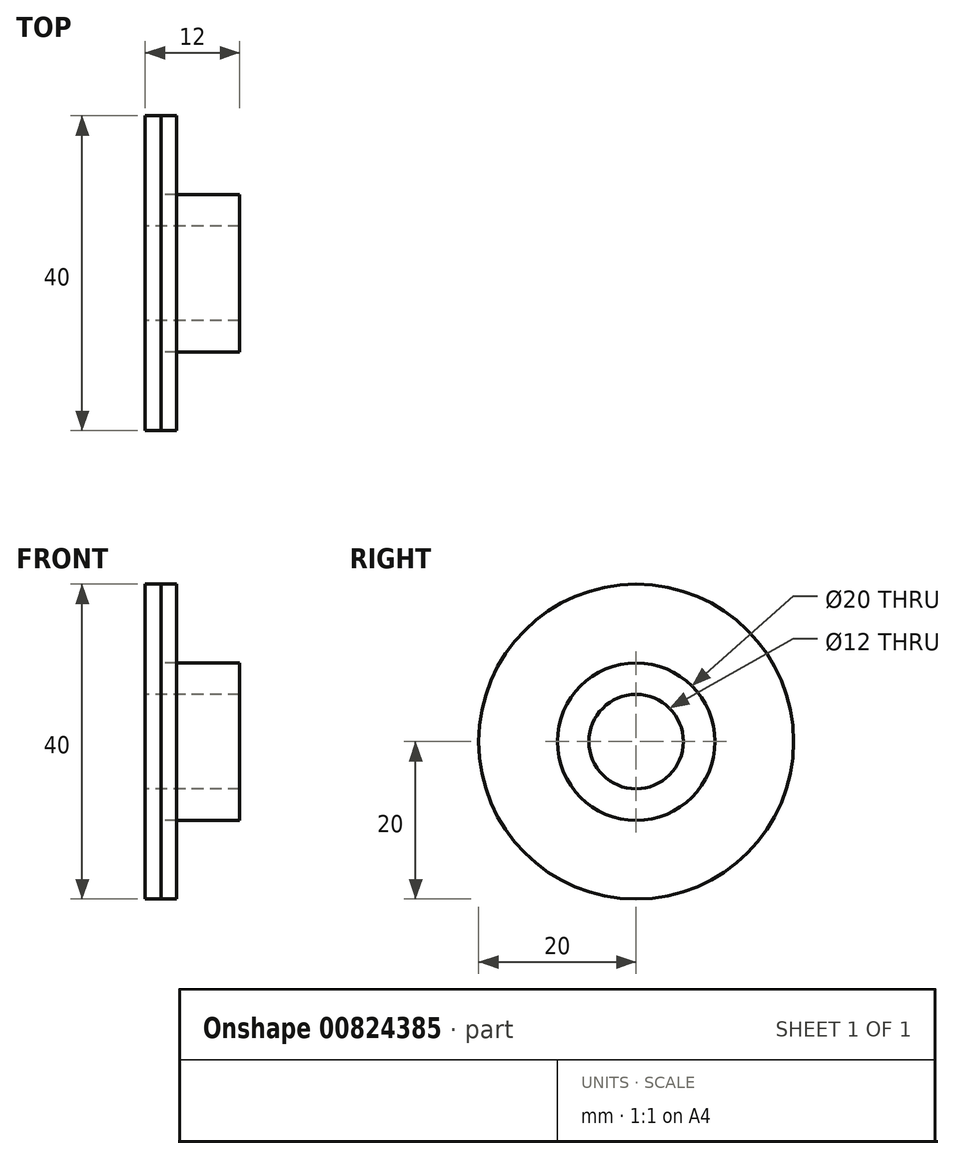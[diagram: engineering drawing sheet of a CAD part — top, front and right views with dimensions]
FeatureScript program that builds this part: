
annotation { "Feature Type Name" : "Feature", "Feature Type Description" : "" }
export const myFeature = defineFeature(function(context is Context, id is Id, definition is map)
    precondition{}
    {
        {
            var Q0;
            Q0=qCreatedBy(makeId("Front.planeOp"),FACE);
            var sketch = newSketch(context, id + "F0", { "sketchPlane" : qUnion([Q0])});
            skLineSegment(sketch, "E0", {"start": v(0, 6) * mm, "end": v(0, 20) * mm});
            skLineSegment(sketch, "E1", {"start": v(0, 20) * mm, "end": v(2, 20) * mm});
            skLineSegment(sketch, "E2", {"start": v(2, 20) * mm, "end": v(2, 10) * mm});
            skLineSegment(sketch, "E3", {"start": v(2, 10) * mm, "end": v(12, 10) * mm});
            skLineSegment(sketch, "E4", {"start": v(12, 10) * mm, "end": v(12, 6) * mm});
            skLineSegment(sketch, "E5", {"start": v(12, 6) * mm, "end": v(0, 6) * mm});
            skLineSegment(sketch, "E6", {"start": v(0, 0) * mm, "end": v(513.86, 0) * mm, "construction": true});
            skSolve(sketch);
        }
        {
            var Q0;
            Q0 = qSketchRegion(id + "F0", true);
            var Q1;
            Q1 = qConstructionFilter(qBodyType(qCreatedBy(id + "F0" ,EDGE), BodyType.WIRE), ConstructionObject.NO);
            var Q2;
            Q2=sQuery(id+"F0.wireOp",EDGE,"E6");
            revolve(context, id + "F1", {"surfaceOperationType" : NewSurfaceOperationType.NEW, "entities" : qUnion([Q0]), "surfaceEntities" : qUnion([Q1]), "axis" : qUnion([Q2]), "revolveType" : RevolveType.FULL});
        }
        {
            var Q0;
            Q0=makeQuery(id+"F1.opRevolve","SWEPT_FACE",FACE,{"disambiguationData":[OSD([sQuery(id+"F0.wireOp",EDGE,"E2")])]});
            var sketch = newSketch(context, id + "F2", { "sketchPlane" : qUnion([Q0])});
            skCircle(sketch, "E7.0", {"center": v(0, 0) * mm, "radius": 20 * mm});
            skCircle(sketch, "E8.0", {"center": v(0, 0) * mm, "radius": 10 * mm});
            skSolve(sketch);
        }
        {
            var Q0;
            Q0 = qSketchRegion(id + "F2", true);
            extrude(context, id + "F3", {"entities" : qUnion([Q0]), "depth" : 2 * mm, "offsetDistance" : 25 * mm});
        }
    });
